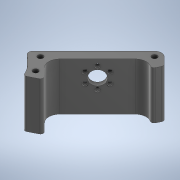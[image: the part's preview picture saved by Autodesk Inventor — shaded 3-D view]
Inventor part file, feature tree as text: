
AUTODESK INVENTOR PART (.ipt)
format: ipt  version: 2020 (Build 240168000, 168)  size: 685,056 bytes
history: native  units: mm
features: extrude x6, sketch x5, other x1, chamfer x1, fillet x1, projected_geometry x1
ambient origin geometry x8: Origin, YZ Plane, XZ Plane, XY Plane, X Axis, Y Axis, Z Axis, Center Point
bodies: Body1 (feature_tree)
feature tree (15):
  other  "Твердое тело1"
  sketch  "Эскиз1"
  extrude  "Выдавливание10"  Depth=3.8mm
  sketch  "Эскиз6"
  extrude  "Выдавливание13"  Depth=6.0mm
  extrude  "Выдавливание14"  Depth=35.0mm TaperAngle=0.0deg
  chamfer  "Фаска3"  Distance=59.0mm
  extrude  "Выдавливание15"  Depth=21.2mm
  fillet  "Сопряжение1"  Radius=15.0mm
  extrude  "Выдавливание16"  Depth=10.4mm
  extrude  "Выдавливание17"  Depth=2.5mm
  sketch  "Эскиз7"
  sketch  "Эскиз8"
  projected_geometry  "Спроецированная петля3"
  sketch  "Эскиз9"
